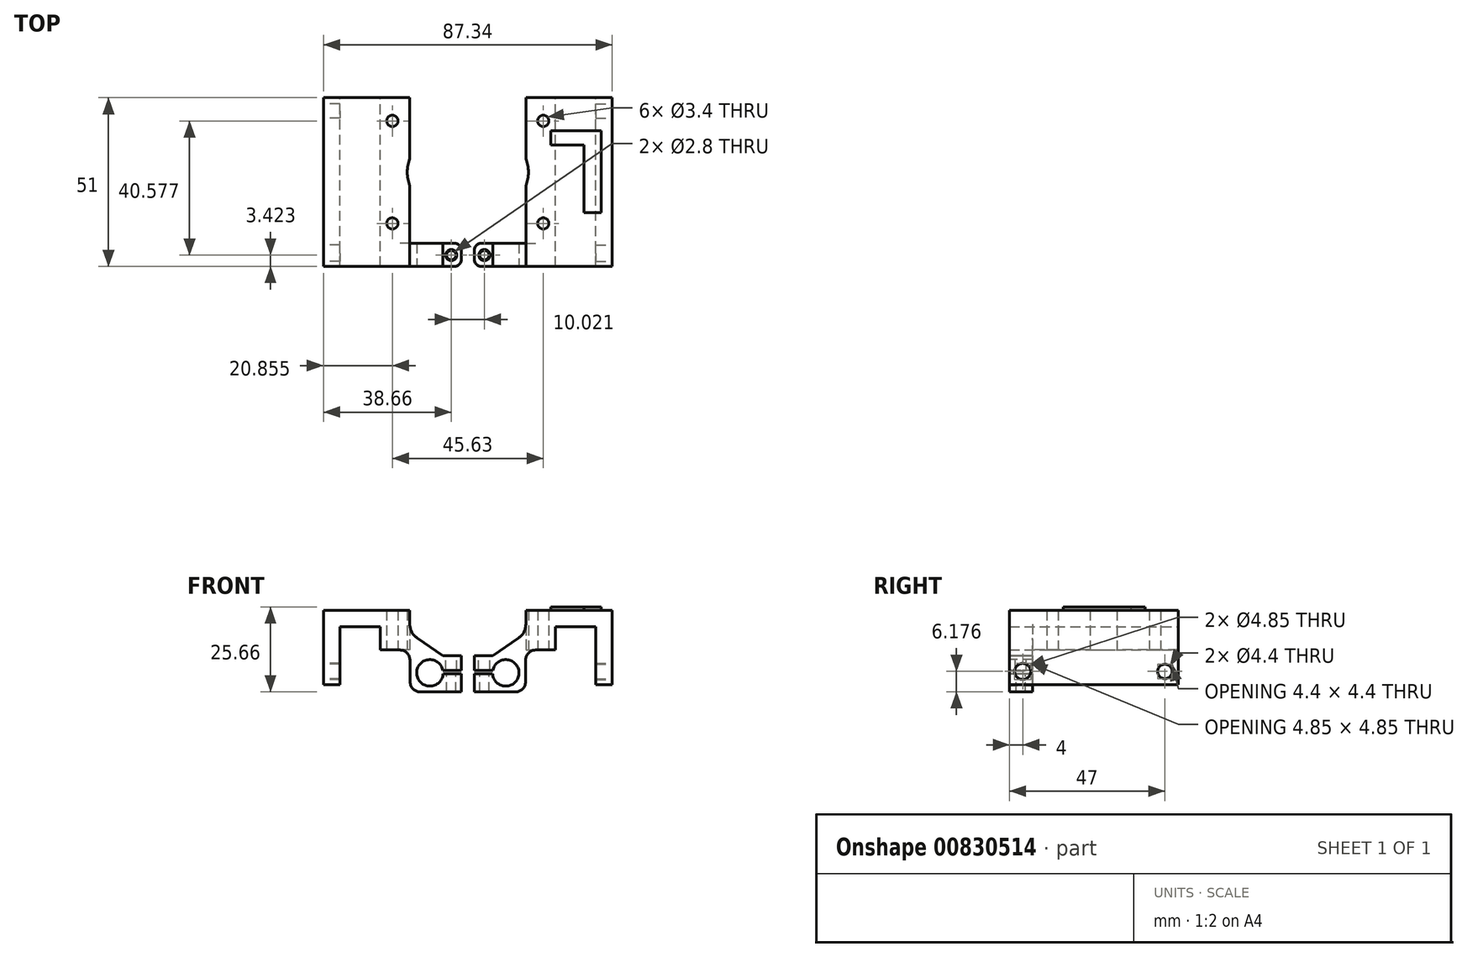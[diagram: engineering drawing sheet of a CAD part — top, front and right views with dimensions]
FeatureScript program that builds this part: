
annotation { "Feature Type Name" : "Feature", "Feature Type Description" : "" }
export const myFeature = defineFeature(function(context is Context, id is Id, definition is map)
    precondition{}
    {
        {
            var Q0;
            Q0=qCreatedBy(makeId("Front.planeOp"),FACE);
            var sketch = newSketch(context, id + "F0", { "sketchPlane" : qUnion([Q0])});
            skLineSegment(sketch, "E0", {"start": v(-18.67, 7.33) * mm, "end": v(-18.67, 29.8) * mm});
            skLineSegment(sketch, "E1", {"start": v(-18.67, 29.8) * mm, "end": v(7.46, 29.8) * mm});
            skLineSegment(sketch, "E2", {"start": v(7.46, 29.8) * mm, "end": v(7.46, 22.94) * mm});
            skLineSegment(sketch, "E3", {"start": v(-1.47, 17.8) * mm, "end": v(-1.47, 24.8) * mm});
            skLineSegment(sketch, "E4", {"start": v(-1.47, 24.8) * mm, "end": v(-13.67, 24.8) * mm});
            skLineSegment(sketch, "E5", {"start": v(-13.67, 24.8) * mm, "end": v(-13.67, 7.33) * mm});
            skLineSegment(sketch, "E6", {"start": v(-13.67, 7.33) * mm, "end": v(-18.67, 7.33) * mm});
            skLineSegment(sketch, "E7", {"start": v(7.46, 22.94) * mm, "end": v(7.46, 17.8) * mm});
            skLineSegment(sketch, "E8", {"start": v(7.46, 17.8) * mm, "end": v(-1.47, 17.8) * mm});
            skLineSegment(sketch, "E9", {"start": v(7.46, 22.94) * mm, "end": v(7.46, 22.94) * mm});
            skLineSegment(sketch, "E10", {"start": v(22.99, 16.14) * mm, "end": v(22.99, 11.7) * mm});
            skLineSegment(sketch, "E11", {"start": v(22.99, 11.7) * mm, "end": v(15.69, 11.7) * mm});
            skLineSegment(sketch, "E12", {"start": v(15.69, 11.7) * mm, "end": v(15.69, 10.67) * mm});
            skLineSegment(sketch, "E13", {"start": v(15.69, 10.67) * mm, "end": v(23.02, 10.67) * mm});
            skLineSegment(sketch, "E14", {"start": v(23.02, 10.67) * mm, "end": v(23.02, 5.15) * mm});
            skLineSegment(sketch, "E15", {"start": v(23.02, 5.15) * mm, "end": v(7.6, 5.15) * mm});
            skLineSegment(sketch, "E16", {"start": v(7.6, 5.15) * mm, "end": v(7.46, 17.8) * mm});
            skLineSegment(sketch, "E17", {"start": v(22.99, 16.14) * mm, "end": v(17.43, 16.14) * mm});
            skLineSegment(sketch, "E18", {"start": v(17.43, 16.14) * mm, "end": v(7.46, 22.94) * mm});
            skSolve(sketch);
        }
        {
            var Q0;
            Q0=makeQuery(id+"F0.imprint","IMPRINT",FACE,{"disambiguationData":[TD([[makeQuery(id+"F0.imprint","IMPRINT",EDGE,{"derivedFrom":sQuery(id+"F0.wireOp",EDGE,"E0")}),-1.0]])]});
            var Q1;
            {var subQ2=sQuery(id+"F0.wireOp",EDGE,"69cbcc5d-e0c3-48db-8baf-3487a8abab7d");Q1=makeQuery(id+"F0.imprint","IMPRINT",FACE,{"disambiguationData":[TD([[makeQuery(id+"F0.imprint","IMPRINT",EDGE,{"derivedFrom":subQ2}),-1.0]])]});}
            var Q2;
            Q2=makeQuery(id+"F0.imprint","IMPRINT",FACE,{"disambiguationData":[TD([[makeQuery(id+"F0.imprint","IMPRINT",EDGE,{"derivedFrom":sQuery(id+"F0.wireOp",EDGE,"E7")}),1.0]])]});
            extrude(context, id + "F1", {"entities" : qUnion([Q0, Q1, Q2]), "depth" : 7 * mm});
        }
        {
            var Q0;
            Q0=makeQuery(id+"F0.imprint","IMPRINT",FACE,{"disambiguationData":[TD([[makeQuery(id+"F0.imprint","IMPRINT",EDGE,{"derivedFrom":sQuery(id+"F0.wireOp",EDGE,"E0")}),-1.0]])]});
            extrude(context, id + "F2", {"entities" : qUnion([Q0]), "operationType" : NewBodyOperationType.ADD, "oppositeDirection" : true, "depth" : 44 * mm, "offsetDistance" : 25 * mm});
        }
        {
            var Q0;
            {var subQ0=sQuery(id+"F0.wireOp",EDGE,"E8");Q0=makeQuery(id+"F2.boolean.opBoolean","MERGE",FACE,{"derivedFrom":[makeQuery(id+"F1.opExtrude","SWEPT_FACE",FACE,{"disambiguationData":[OSD([subQ0])]}),makeQuery(id+"F2.opExtrude","SWEPT_FACE",FACE,{"disambiguationData":[OSD([subQ0])]})]});}
            var sketch = newSketch(context, id + "F3", { "sketchPlane" : qUnion([Q0])});
            skCircle(sketch, "E19", {"center": v(2.19, -6) * mm, "radius": 1.7 * mm});
            skCircle(sketch, "E20", {"center": v(2.19, -37) * mm, "radius": 1.7 * mm});
            skCircle(sketch, "E21", {"center": v(17.69, -21.5) * mm, "radius": 11 * mm});
            skSolve(sketch);
        }
        {
            var Q0;
            Q0=qSketchRegion(id+"F3",true);
            extrude(context, id + "F4", {"entities" : qUnion([Q0]), "operationType" : NewBodyOperationType.REMOVE, "endBound" : BoundingType.THROUGH_ALL, "oppositeDirection" : true, "depth" : 25 * mm});
        }
        {
            var Q0;
            Q0=makeQuery(id+"F1.opExtrude","CAP_FACE",FACE,{"disambiguationData":[OSD([sQuery(id+"F0.wireOp",EDGE,"E0"),sQuery(id+"F0.wireOp",EDGE,"E1"),sQuery(id+"F0.wireOp",EDGE,"E2"),sQuery(id+"F0.wireOp",EDGE,"E3"),sQuery(id+"F0.wireOp",EDGE,"E4"),sQuery(id+"F0.wireOp",EDGE,"E5"),sQuery(id+"F0.wireOp",EDGE,"E6"),sQuery(id+"F0.wireOp",EDGE,"E8"),sQuery(id+"F0.wireOp",EDGE,"E9"),sQuery(id+"F0.wireOp",EDGE,"58f11638-63e7-4b32-8aff-a1ba3c53649b"),sQuery(id+"F0.wireOp",EDGE,"E10"),sQuery(id+"F0.wireOp",EDGE,"E11"),sQuery(id+"F0.wireOp",EDGE,"E12"),sQuery(id+"F0.wireOp",EDGE,"E13"),sQuery(id+"F0.wireOp",EDGE,"E14"),sQuery(id+"F0.wireOp",EDGE,"E15"),sQuery(id+"F0.wireOp",EDGE,"E16")])],"isStart":false});
            var sketch = newSketch(context, id + "F5", { "sketchPlane" : qUnion([Q0])});
            skCircle(sketch, "E22", {"center": v(13.53, 10.9) * mm, "radius": 4 * mm});
            skSolve(sketch);
        }
        {
            var Q0;
            Q0=qSketchRegion(id+"F5",true);
            extrude(context, id + "F6", {"entities" : qUnion([Q0]), "operationType" : NewBodyOperationType.REMOVE, "oppositeDirection" : true, "depth" : 10 * mm});
        }
        {
            var Q0;
            Q0=qSketchRegion(id+"F3",true);
            extrude(context, id + "F7", {"entities" : qUnion([Q0]), "operationType" : NewBodyOperationType.REMOVE, "endBound" : BoundingType.THROUGH_ALL, "oppositeDirection" : true, "depth" : 25 * mm});
        }
        {
            var Q0;
            Q0=makeQuery(id+"F1.opExtrude","SWEPT_FACE",FACE,{"disambiguationData":[OSD([sQuery(id+"F0.wireOp",EDGE,"E17")])]});
            var sketch = newSketch(context, id + "F8", { "sketchPlane" : qUnion([Q0])});
            skCircle(sketch, "E23", {"center": v(19.99, -3.58) * mm, "radius": 1.7 * mm});
            skCircle(sketch, "E24", {"center": v(19.99, -3.58) * mm, "radius": 1.4 * mm});
            skSolve(sketch);
        }
        {
            var Q0;
            Q0=makeQuery(id+"F8.imprint","IMPRINT",FACE,{"disambiguationData":[TD([[makeQuery(id+"F8.imprint","IMPRINT",EDGE,{"derivedFrom":sQuery(id+"F8.wireOp",EDGE,"E24")}),1.0]])]});
            extrude(context, id + "F9", {"entities" : qUnion([Q0]), "operationType" : NewBodyOperationType.REMOVE, "endBound" : BoundingType.THROUGH_ALL, "oppositeDirection" : true, "depth" : 25 * mm});
        }
        {
            var Q0;
            Q0=makeQuery(id+"F8.imprint","IMPRINT",FACE,{"disambiguationData":[TD([[makeQuery(id+"F8.imprint","IMPRINT",EDGE,{"derivedFrom":sQuery(id+"F8.wireOp",EDGE,"E23")}),1.0]])]});
            extrude(context, id + "F10", {"entities" : qUnion([Q0]), "operationType" : NewBodyOperationType.REMOVE, "endBound" : BoundingType.UP_TO_NEXT, "oppositeDirection" : true, "depth" : 25 * mm});
        }
        {
            var Q0;
            Q0=makeQuery(id+"F1.opExtrude","SWEPT_EDGE",EDGE,{"disambiguationData":[OSD([sQuery(id+"F0.wireOp",EDGE,"E2"),sQuery(id+"F0.wireOp",EDGE,"E7"),sQuery(id+"F0.wireOp",EDGE,"E18")])]});
            fillet(context, id + "F11", {"entities" : qUnion([Q0]), "radius" : 5 * mm, "tangentPropagation" : true, "allowEdgeOverflow" : false});
        }
        {
            var Q0;
            Q0=makeQuery(id+"F1.opExtrude","SWEPT_EDGE",EDGE,{"disambiguationData":[OSD([sQuery(id+"F0.wireOp",EDGE,"E7"),sQuery(id+"F0.wireOp",EDGE,"E8"),sQuery(id+"F0.wireOp",EDGE,"E16")])]});
            fillet(context, id + "F12", {"entities" : qUnion([Q0]), "radius" : 3 * mm, "tangentPropagation" : true, "allowEdgeOverflow" : false});
        }
        {
            var Q0;
            Q0=makeQuery(id+"F1.opExtrude","SWEPT_EDGE",EDGE,{"disambiguationData":[OSD([sQuery(id+"F0.wireOp",EDGE,"E15"),sQuery(id+"F0.wireOp",EDGE,"E16")])]});
            fillet(context, id + "F13", {"entities" : qUnion([Q0]), "radius" : 3 * mm, "tangentPropagation" : true, "allowEdgeOverflow" : false});
        }
        {
            var Q0;
            Q0=makeQuery(id+"F1.opExtrude","CAP_EDGE",EDGE,{"disambiguationData":[OSD([sQuery(id+"F0.wireOp",EDGE,"E10")])],"isStart":false});
            var Q1;
            Q1=makeQuery(id+"F1.opExtrude","CAP_EDGE",EDGE,{"disambiguationData":[OSD([sQuery(id+"F0.wireOp",EDGE,"E14")])],"isStart":false});
            var Q2;
            Q2=makeQuery(id+"F1.opExtrude","CAP_EDGE",EDGE,{"disambiguationData":[OSD([sQuery(id+"F0.wireOp",EDGE,"E10")])],"isStart":true});
            var Q3;
            Q3=makeQuery(id+"F1.opExtrude","CAP_EDGE",EDGE,{"disambiguationData":[OSD([sQuery(id+"F0.wireOp",EDGE,"E14")])],"isStart":true});
            fillet(context, id + "F14", {"entities" : qUnion([Q0, Q1, Q2, Q3]), "radius" : 2 * mm, "tangentPropagation" : true, "allowEdgeOverflow" : false});
        }
        {
            var Q0;
            {var subQ0=sQuery(id+"F0.wireOp",EDGE,"E0");Q0=makeQuery(id+"F2.boolean.opBoolean","MERGE",FACE,{"derivedFrom":[makeQuery(id+"F1.opExtrude","SWEPT_FACE",FACE,{"disambiguationData":[OSD([subQ0])]}),makeQuery(id+"F2.opExtrude","SWEPT_FACE",FACE,{"disambiguationData":[OSD([subQ0])]})]});}
            var sketch = newSketch(context, id + "F15", { "sketchPlane" : qUnion([Q0])});
            skCircle(sketch, "E25", {"center": v(-40, 11.33) * mm, "radius": 2.2 * mm});
            skCircle(sketch, "E26", {"center": v(3, 11.33) * mm, "radius": 2.43 * mm});
            skSolve(sketch);
        }
        {
            var Q0;
            Q0=qSketchRegion(id+"F15",true);
            extrude(context, id + "F16", {"entities" : qUnion([Q0]), "operationType" : NewBodyOperationType.REMOVE, "oppositeDirection" : true, "depth" : 6 * mm});
        }
        {
            var Q0;
            Q0=makeQuery(id+"F1.opExtrude","SWEPT_BODY",BODY,{"disambiguationData":[OSD([sQuery(id+"F0.wireOp",EDGE,"E0"),sQuery(id+"F0.wireOp",EDGE,"E1"),sQuery(id+"F0.wireOp",EDGE,"E2"),sQuery(id+"F0.wireOp",EDGE,"E3"),sQuery(id+"F0.wireOp",EDGE,"E4"),sQuery(id+"F0.wireOp",EDGE,"E5"),sQuery(id+"F0.wireOp",EDGE,"E6"),sQuery(id+"F0.wireOp",EDGE,"E8"),sQuery(id+"F0.wireOp",EDGE,"E10"),sQuery(id+"F0.wireOp",EDGE,"E11"),sQuery(id+"F0.wireOp",EDGE,"E12"),sQuery(id+"F0.wireOp",EDGE,"E13"),sQuery(id+"F0.wireOp",EDGE,"E14"),sQuery(id+"F0.wireOp",EDGE,"E15"),sQuery(id+"F0.wireOp",EDGE,"E16"),sQuery(id+"F0.wireOp",EDGE,"E17"),sQuery(id+"F0.wireOp",EDGE,"E18")])]});
            var Q1;
            Q1=qCreatedBy(makeId("Right.planeOp"),FACE);
            mirror(context, id + "F17", {"entities" : qUnion([Q0]), "mirrorPlane" : qUnion([Q1])});
        }
        {
            var Q0;
            Q0=makeQuery(id+"F17.opPattern","COPY",BODY,{"derivedFrom":makeQuery(id+"F1.opExtrude","SWEPT_BODY",BODY,{"disambiguationData":[OSD([sQuery(id+"F0.wireOp",EDGE,"E0"),sQuery(id+"F0.wireOp",EDGE,"E1"),sQuery(id+"F0.wireOp",EDGE,"E2"),sQuery(id+"F0.wireOp",EDGE,"E3"),sQuery(id+"F0.wireOp",EDGE,"E4"),sQuery(id+"F0.wireOp",EDGE,"E5"),sQuery(id+"F0.wireOp",EDGE,"E6"),sQuery(id+"F0.wireOp",EDGE,"E8"),sQuery(id+"F0.wireOp",EDGE,"E10"),sQuery(id+"F0.wireOp",EDGE,"E11"),sQuery(id+"F0.wireOp",EDGE,"E12"),sQuery(id+"F0.wireOp",EDGE,"E13"),sQuery(id+"F0.wireOp",EDGE,"E14"),sQuery(id+"F0.wireOp",EDGE,"E15"),sQuery(id+"F0.wireOp",EDGE,"E16"),sQuery(id+"F0.wireOp",EDGE,"E17"),sQuery(id+"F0.wireOp",EDGE,"E18")])]}),"instanceName":"1"});
            transform(context, id + "F18", {"entities" : qUnion([Q0]), "transformType" : TransformType.TRANSLATION_3D, "dx" : 50 * mm, "dy" : 0 * mm, "dz" : 0 * mm, "makeCopy" : false});
        }
        {
            var Q0;
            {var subQ0=sQuery(id+"F0.wireOp",EDGE,"E1");Q0=makeQuery(id+"F17.opPattern","COPY",FACE,{"derivedFrom":makeQuery(id+"F2.boolean.opBoolean","MERGE",FACE,{"derivedFrom":[makeQuery(id+"F1.opExtrude","SWEPT_FACE",FACE,{"disambiguationData":[OSD([subQ0])]}),makeQuery(id+"F2.opExtrude","SWEPT_FACE",FACE,{"disambiguationData":[OSD([subQ0])]})]}),"instanceName":"1"});}
            var sketch = newSketch(context, id + "F19", { "sketchPlane" : qUnion([Q0])});
            skText(sketch, "E27", { "text": "L", "fontName": "OpenSans-Bold.ttf"});
            skLineSegment(sketch, "E28", {"start": v(47.81, 37) * mm, "end": v(47.81, 6) * mm, "construction": true});
            skPoint(sketch, "E29", {"position": v(47.81, 21.5) * mm});
            const initialGuessF19  = {"E27": [0.0685, 0.034, -1, 0, 0.025]};
            skSetInitialGuess(sketch, initialGuessF19);
            skSolve(sketch);
        }
        {
            var Q0;
            Q0=qSketchRegion(id+"F19",true);
            extrude(context, id + "F20", {"entities" : qUnion([Q0]), "operationType" : NewBodyOperationType.ADD, "depth" : 1 * mm, "offsetDistance" : 25 * mm});
        }
    });
